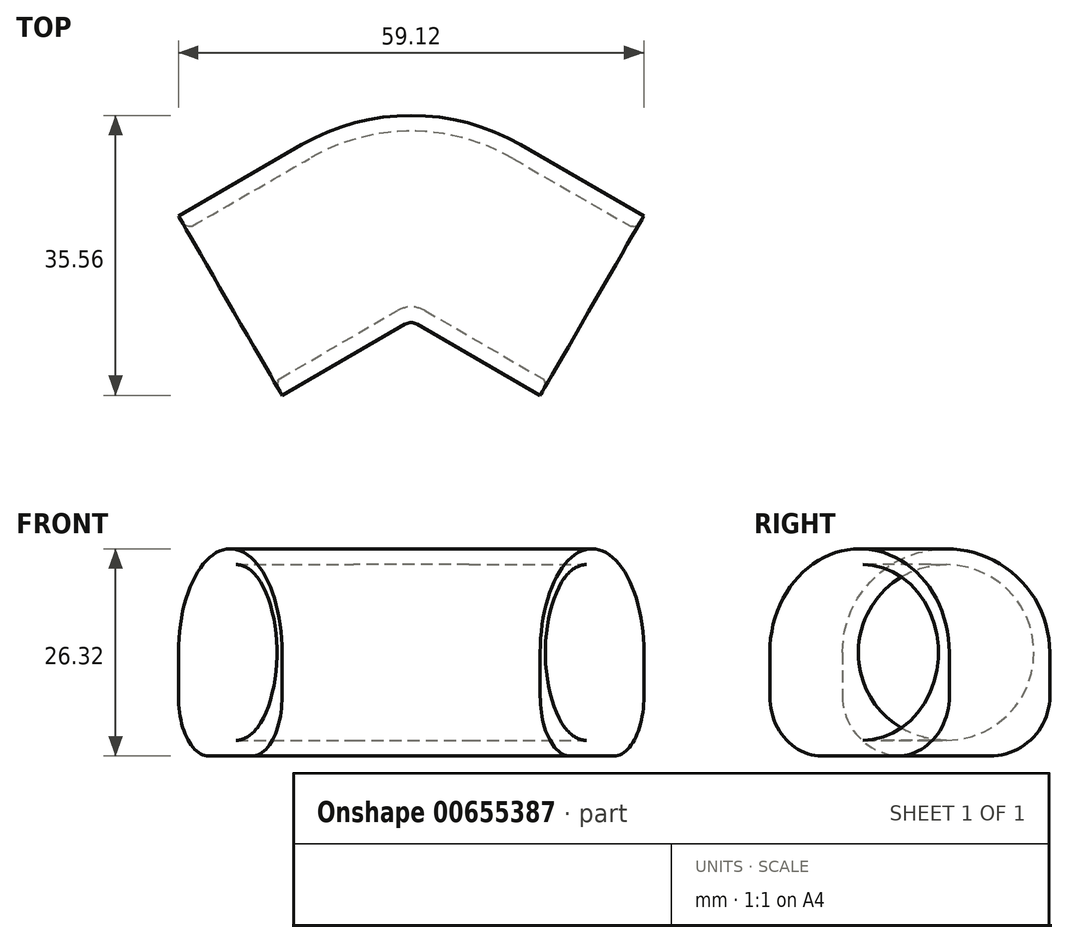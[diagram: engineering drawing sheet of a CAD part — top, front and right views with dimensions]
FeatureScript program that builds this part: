
annotation { "Feature Type Name" : "Feature", "Feature Type Description" : "" }
export const myFeature = defineFeature(function(context is Context, id is Id, definition is map)
    precondition{}
    {
        {
            var Q0;
            Q0=qCreatedBy(makeId("Top.planeOp"),FACE);
            var sketch = newSketch(context, id + "F0", { "sketchPlane" : qUnion([Q0])});
            skLineSegment(sketch, "E0", {"start": v(0, 0) * mm, "end": v(0, -12.7) * mm, "construction": true});
            skLineSegment(sketch, "E1", {"start": v(-22, -12.7) * mm, "end": v(0, -12.7) * mm, "construction": true});
            skLineSegment(sketch, "E2", {"start": v(-22, -12.7) * mm, "end": v(-6.35, -3.67) * mm});
            skLineSegment(sketch, "E3.MirrorCS", {"start": v(22, -12.7) * mm, "end": v(6.35, -3.67) * mm});
            skLineSegment(sketch, "E4.MirrorCS", {"start": v(22, -12.7) * mm, "end": v(0, -12.7) * mm, "construction": true});
            skPoint(sketch, "E5.visualSharp", {"position": v(0, 0) * mm});
            skArc(sketch, "E5.filletArc", {"start": v(6.35, -3.67) * mm, "mid": v(0, -1.96) * mm, "end": v(-6.35, -3.67) * mm});
            skSolve(sketch);
        }
        {
            var Q0;
            Q0=qCreatedBy(makeId("Right.planeOp"),FACE);
            var sketch = newSketch(context, id + "F1", { "sketchPlane" : qUnion([Q0])});
            skCircle(sketch, "E6", {"center": v(0, 0) * mm, "radius": 11.16 * mm});
            skCircle(sketch, "E7.0", {"center": v(0, 0) * mm, "radius": 13.16 * mm});
            skLineSegment(sketch, "E8.bottom", {"start": v(13.16, 0) * mm, "end": v(-13.16, 0) * mm, "construction": true});
            skLineSegment(sketch, "E8.left", {"start": v(13.16, 0) * mm, "end": v(13.16, -13.16) * mm});
            skLineSegment(sketch, "E8.right", {"start": v(-13.16, 0) * mm, "end": v(-13.16, -13.16) * mm});
            skPoint(sketch, "E8.middle", {"position": v(0, -13.16) * mm});
            skLineSegment(sketch, "E9", {"start": v(0, -13.16) * mm, "end": v(-13.16, -13.16) * mm});
            skLineSegment(sketch, "E10", {"start": v(0, -13.16) * mm, "end": v(13.16, -13.16) * mm});
            skSolve(sketch);
        }
        {
            var Q0;
            Q0 = qSketchRegion(id + "F1", true);
            var Q1;
            Q1 = qConstructionFilter(qBodyType(qCreatedBy(id + "F0" ,EDGE), BodyType.WIRE), ConstructionObject.NO);
            sweep(context, id + "F2", {"profiles" : qUnion([Q0]), "path" : qUnion([Q1])});
        }
        {
            var Q0;
            Q0=makeQuery(id+"F2.opSweep","SWEPT_EDGE",EDGE,{"disambiguationData":[OSD([sQuery(id+"F0.wireOp",EDGE,"E2"),sQuery(id+"F1.wireOp",EDGE,"E8.right"),sQuery(id+"F1.wireOp",EDGE,"E9")])]});
            var Q1;
            Q1=makeQuery(id+"F2.opSweep","SWEPT_EDGE",EDGE,{"disambiguationData":[OSD([sQuery(id+"F0.wireOp",EDGE,"E3.MirrorCS"),sQuery(id+"F1.wireOp",EDGE,"E8.right"),sQuery(id+"F1.wireOp",EDGE,"E9")])]});
            var Q2;
            Q2=makeQuery(id+"F2.opSweep","SWEPT_EDGE",EDGE,{"disambiguationData":[OSD([sQuery(id+"F0.wireOp",EDGE,"E5.filletArc"),sQuery(id+"F1.wireOp",EDGE,"E8.right"),sQuery(id+"F1.wireOp",EDGE,"E9")])]});
            var Q3;
            Q3=makeQuery(id+"F2.opSweep","SWEPT_EDGE",EDGE,{"disambiguationData":[OSD([sQuery(id+"F0.wireOp",EDGE,"E3.MirrorCS"),sQuery(id+"F1.wireOp",EDGE,"E8.left"),sQuery(id+"F1.wireOp",EDGE,"E10")])]});
            var Q4;
            Q4=makeQuery(id+"F2.opSweep","SWEPT_EDGE",EDGE,{"disambiguationData":[OSD([sQuery(id+"F0.wireOp",EDGE,"E5.filletArc"),sQuery(id+"F1.wireOp",EDGE,"E8.left"),sQuery(id+"F1.wireOp",EDGE,"E10")])]});
            var Q5;
            Q5=makeQuery(id+"F2.opSweep","SWEPT_EDGE",EDGE,{"disambiguationData":[OSD([sQuery(id+"F0.wireOp",EDGE,"E2"),sQuery(id+"F1.wireOp",EDGE,"E8.left"),sQuery(id+"F1.wireOp",EDGE,"E10")])]});
            fillet(context, id + "F3", {"entities" : qUnion([Q0, Q1, Q2, Q3, Q4, Q5]), "radius" : 7.62 * mm, "tangentPropagation" : true, "allowEdgeOverflow" : false});
        }
        {
            var Q0;
            Q0=makeQuery(id+"F2.opSweep","CAP_EDGE",EDGE,{"disambiguationData":[OSD([sQuery(id+"F0.wireOp",VERTEX,"E3.MirrorCS.start"),sQuery(id+"F1.wireOp",EDGE,"E6")])],"isStart":false});
            var Q1;
            Q1=makeQuery(id+"F2.opSweep","CAP_EDGE",EDGE,{"disambiguationData":[OSD([sQuery(id+"F0.wireOp",VERTEX,"E2.start"),sQuery(id+"F1.wireOp",EDGE,"E6")])],"isStart":true});
            chamfer(context, id + "F4", {"entities" : qUnion([Q0, Q1]), "width" : 0.64 * mm, "tangentPropagation" : true});
        }
        {
            var Q0;
            {var subQ0=sQuery(id+"F1.wireOp",EDGE,"E6");Q0=makeQuery(id+"F4.opChamfer","BLEND_EDGE",EDGE,{"blendedFrom":[makeQuery(id+"F2.opSweep","CAP_EDGE",EDGE,{"disambiguationData":[OSD([sQuery(id+"F0.wireOp",VERTEX,"E2.start"),subQ0])],"isStart":true}),makeQuery(id+"F2.opSweep","SWEPT_FACE",FACE,{"disambiguationData":[OSD([sQuery(id+"F0.wireOp",EDGE,"E2"),subQ0])]})],"blendedInto":[makeQuery(id+"F2.opSweep","SWEPT_FACE",FACE,{"disambiguationData":[OSD([sQuery(id+"F0.wireOp",EDGE,"E2"),subQ0])]})]});}
            var Q1;
            {var subQ0=sQuery(id+"F1.wireOp",EDGE,"E6");var subQ1=sQuery(id+"F0.wireOp",VERTEX,"E2.start");Q1=makeQuery(id+"F4.opChamfer","BLEND_EDGE",EDGE,{"blendedFrom":[makeQuery(id+"F2.opSweep","CAP_EDGE",EDGE,{"disambiguationData":[OSD([subQ1,subQ0])],"isStart":true}),makeQuery(id+"F2.opSweep","CAP_FACE",FACE,{"disambiguationData":[OSD([subQ1,subQ0,sQuery(id+"F1.wireOp",EDGE,"E7.0"),sQuery(id+"F1.wireOp",EDGE,"E8.left"),sQuery(id+"F1.wireOp",EDGE,"E8.right"),sQuery(id+"F1.wireOp",EDGE,"E9"),sQuery(id+"F1.wireOp",EDGE,"E10")])],"isStart":true})],"blendedInto":[makeQuery(id+"F2.opSweep","CAP_FACE",FACE,{"disambiguationData":[OSD([subQ1,subQ0,sQuery(id+"F1.wireOp",EDGE,"E7.0"),sQuery(id+"F1.wireOp",EDGE,"E8.left"),sQuery(id+"F1.wireOp",EDGE,"E8.right"),sQuery(id+"F1.wireOp",EDGE,"E9"),sQuery(id+"F1.wireOp",EDGE,"E10")])],"isStart":true})]});}
            var Q2;
            {var subQ0=sQuery(id+"F1.wireOp",EDGE,"E6");var subQ1=sQuery(id+"F0.wireOp",VERTEX,"E3.MirrorCS.start");Q2=makeQuery(id+"F4.opChamfer","BLEND_EDGE",EDGE,{"blendedFrom":[makeQuery(id+"F2.opSweep","CAP_EDGE",EDGE,{"disambiguationData":[OSD([subQ1,subQ0])],"isStart":false}),makeQuery(id+"F2.opSweep","CAP_FACE",FACE,{"disambiguationData":[OSD([subQ1,subQ0,sQuery(id+"F1.wireOp",EDGE,"E7.0"),sQuery(id+"F1.wireOp",EDGE,"E8.left"),sQuery(id+"F1.wireOp",EDGE,"E8.right"),sQuery(id+"F1.wireOp",EDGE,"E9"),sQuery(id+"F1.wireOp",EDGE,"E10")])],"isStart":false})],"blendedInto":[makeQuery(id+"F2.opSweep","CAP_FACE",FACE,{"disambiguationData":[OSD([subQ1,subQ0,sQuery(id+"F1.wireOp",EDGE,"E7.0"),sQuery(id+"F1.wireOp",EDGE,"E8.left"),sQuery(id+"F1.wireOp",EDGE,"E8.right"),sQuery(id+"F1.wireOp",EDGE,"E9"),sQuery(id+"F1.wireOp",EDGE,"E10")])],"isStart":false})]});}
            var Q3;
            {var subQ0=sQuery(id+"F1.wireOp",EDGE,"E6");Q3=makeQuery(id+"F4.opChamfer","BLEND_EDGE",EDGE,{"blendedFrom":[makeQuery(id+"F2.opSweep","CAP_EDGE",EDGE,{"disambiguationData":[OSD([sQuery(id+"F0.wireOp",VERTEX,"E3.MirrorCS.start"),subQ0])],"isStart":false}),makeQuery(id+"F2.opSweep","SWEPT_FACE",FACE,{"disambiguationData":[OSD([sQuery(id+"F0.wireOp",EDGE,"E3.MirrorCS"),subQ0])]})],"blendedInto":[makeQuery(id+"F2.opSweep","SWEPT_FACE",FACE,{"disambiguationData":[OSD([sQuery(id+"F0.wireOp",EDGE,"E3.MirrorCS"),subQ0])]})]});}
            fillet(context, id + "F5", {"entities" : qUnion([Q0, Q1, Q2, Q3]), "radius" : 0.5 * mm, "tangentPropagation" : true, "allowEdgeOverflow" : false});
        }
    });
